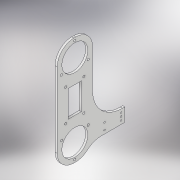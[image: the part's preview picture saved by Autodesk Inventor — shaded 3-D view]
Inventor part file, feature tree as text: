
AUTODESK INVENTOR PART (.ipt)
format: ipt  version: 2019 (Build 230136000, 136)  size: 238,592 bytes
history: native  units: in
note: dims shown in document units (in); Inventor stores cm internally (conversion verified against a paired STEP export)
features: sketch x19, hole x16, extrude x4
ambient origin geometry x8: Origin, YZ Plane, XZ Plane, XY Plane, X Axis, Y Axis, Z Axis, Center Point
bodies: Solid1 (feature_tree)
feature tree (39):
  hole  "Hole1"  [1 undecoded]
  hole  "Hole2"  [1 undecoded]
  hole  "Hole3"  [1 undecoded]
  hole  "Hole4"  [1 undecoded]
  hole  "Hole5"  [1 undecoded]
  hole  "Hole6"  [1 undecoded]
  hole  "Hole7"  [1 undecoded]
  hole  "Hole8"  [1 undecoded]
  hole  "Hole9"  [1 undecoded]
  hole  "Hole10"  [1 undecoded]
  hole  "Hole11"  [1 undecoded]
  hole  "Hole12"  [1 undecoded]
  extrude  "Extrusion1"  [1 undecoded]
  hole  "Hole13"  [1 undecoded]
  extrude  "Extrusion2"  [1 undecoded]
  hole  "Hole14"  [1 undecoded]
  extrude  "Extrusion3"  [1 undecoded]
  hole  "Hole15"  [1 undecoded]
  extrude  "Extrusion4"  [1 undecoded]
  sketch  "Sketch1"  dims[d0=0.266in d1=0.2362in d2=0.507in d3=0.0787in d4=0.563in d5=0.5883in d6=0.8108in]
  sketch  "Sketch2"  dims[d7=0.266in d8=0.2362in d9=0.507in d10=0.0787in d11=0.563in d12=0.5883in d13=0.8108in]
  sketch  "Sketch3"  dims[d14=0.266in d15=0.2362in d16=0.507in d17=0.0787in d18=0.563in d19=0.5883in d20=0.8108in]
  sketch  "Sketch4"  dims[d21=0.266in d22=0.2362in d23=0.507in d24=0.0787in d25=0.563in d26=0.5883in d27=0.8108in]
  sketch  "Sketch5"  dims[d28=0.266in d29=0.2362in d30=0.507in d31=0.0787in d32=0.563in d33=0.5883in d34=0.8108in]
  sketch  "Sketch6"  dims[d35=0.266in d36=0.2362in d37=0.507in d38=0.0787in d39=0.563in d40=0.5883in d41=0.8108in]
  sketch  "Sketch7"  dims[d42=0.266in d43=0.2362in d44=0.507in d45=0.0787in d46=0.563in d47=0.5883in d48=0.8108in]
  sketch  "Sketch8"  dims[d49=0.266in d50=0.2362in d51=0.507in d52=0.0787in d53=0.563in d54=0.5883in d55=0.8108in]
  sketch  "Sketch9"  dims[d56=0.266in d57=0.2362in d58=0.507in d59=0.0787in d60=0.563in d61=0.5883in d62=0.8108in]
  sketch  "Sketch10"  dims[d63=0.266in d64=0.2362in d65=0.507in d66=0.0787in d67=0.563in d68=0.5883in d69=0.8108in]
  sketch  "Sketch11"  dims[d70=0.177in d71=0.2362in d72=0.332in d73=0.0787in d74=0.563in d75=0.5883in d76=0.8108in]
  sketch  "Sketch12"  dims[d77=0.177in d78=0.2362in d79=0.332in d80=0.0787in d81=0.563in d82=0.5883in d83=0.8108in d84=0.3937in d85=0.0in]
  sketch  "Sketch13"  dims[d86=3.0709in d87=0.2362in d88=0.332in d89=0.0787in d90=0.563in d91=3.0709in d92=0.8108in d93=0.3937in d94=0.0in]
  sketch  "Sketch14"  dims[d95=3.0709in d96=0.2362in d97=0.332in d98=0.0787in d99=0.563in d100=3.0709in d101=0.8108in d102=0.3937in d103=0.0in]
  sketch  "Sketch15"  dims[d104=0.201in d105=0.2362in d106=0.385in d107=0.0787in d108=0.563in d109=3.0709in d110=0.8108in d111=0.1437in d112=0.0in]
  sketch  "Sketch16"
  sketch  "Sketch17"
  sketch  "Sketch18"
  sketch  "Sketch19"
  hole  "hole_plate1"  [1 undecoded]
note: 20 required parameter values undecoded (feature->parameter linkage not recoverable at this tier; creation-order binding heuristic only, values carry confidence <= 0.55)
